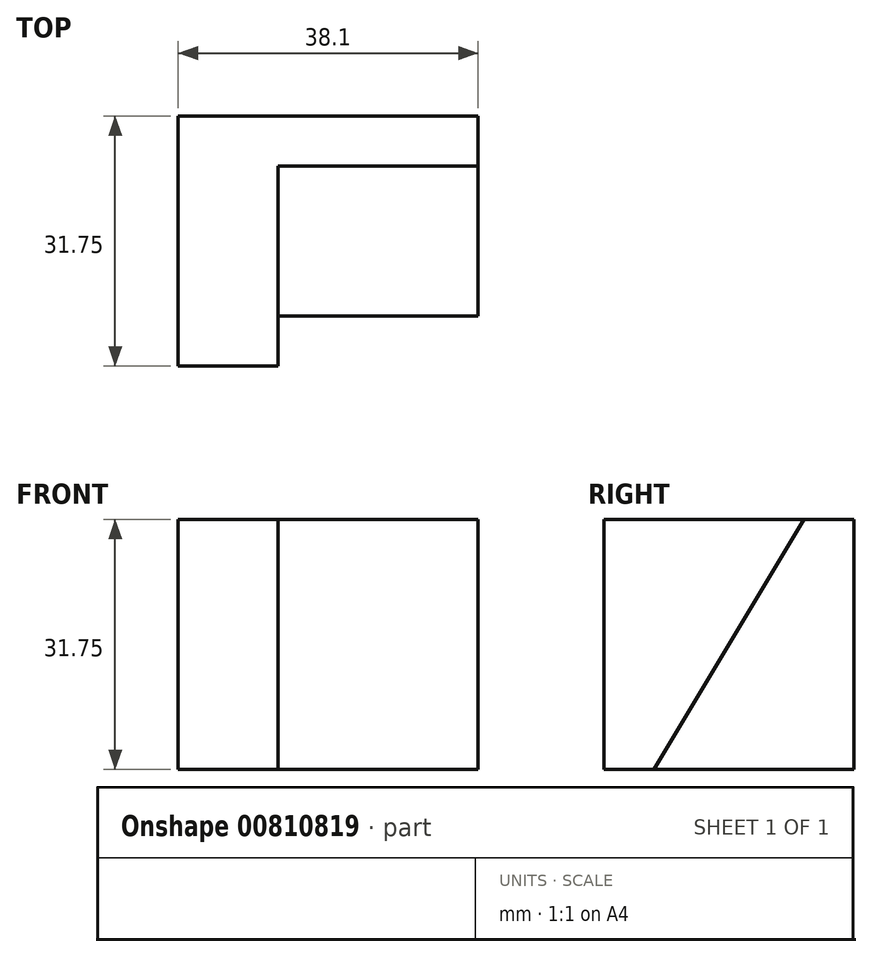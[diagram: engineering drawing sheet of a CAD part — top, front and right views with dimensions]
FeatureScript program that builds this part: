
annotation { "Feature Type Name" : "Feature", "Feature Type Description" : "" }
export const myFeature = defineFeature(function(context is Context, id is Id, definition is map)
    precondition{}
    {
        {
            var Q0;
            Q0=qCreatedBy(makeId("Top.planeOp"),FACE);
            var sketch = newSketch(context, id + "F0", { "sketchPlane" : qUnion([Q0])});
            skLineSegment(sketch, "E0", {"start": v(0, 0) * mm, "end": v(0, 31.75) * mm});
            skLineSegment(sketch, "E1", {"start": v(0, 0) * mm, "end": v(38.1, 0) * mm});
            skLineSegment(sketch, "E2", {"start": v(38.1, 0) * mm, "end": v(38.1, 31.75) * mm});
            skLineSegment(sketch, "E3", {"start": v(38.1, 31.75) * mm, "end": v(0, 31.75) * mm});
            skSolve(sketch);
        }
        {
            var Q0;
            Q0 = qSketchRegion(id + "F0", true);
            extrude(context, id + "F1", {"entities" : qUnion([Q0]), "depth" : 31.75 * mm, "offsetDistance" : 25.4 * mm});
        }
        {
            var Q0;
            Q0=makeQuery(id+"F1.opExtrude","SWEPT_FACE",FACE,{"disambiguationData":[OSD([sQuery(id+"F0.wireOp",EDGE,"E2")])]});
            var sketch = newSketch(context, id + "F2", { "sketchPlane" : qUnion([Q0])});
            skLineSegment(sketch, "E4", {"start": v(31.75, 31.75) * mm, "end": v(25.4, 31.75) * mm});
            skLineSegment(sketch, "E5", {"start": v(0, 0) * mm, "end": v(6.35, 0) * mm});
            skLineSegment(sketch, "E6", {"start": v(25.4, 31.75) * mm, "end": v(6.35, 0) * mm});
            skSolve(sketch);
        }
        {
            var Q0;
            Q0 = qSketchRegion(id + "F2", true);
            var Q1;
            Q1=makeQuery(id+"F2.imprint","IMPRINT",FACE,{"disambiguationData":[TD([[makeQuery(id+"F2.imprint","IMPRINT",EDGE,{"derivedFrom":sQuery(id+"F2.wireOp",EDGE,"E5")}),1.0]])]});
            extrude(context, id + "F3", {"entities" : qUnion([Q0, Q1]), "operationType" : NewBodyOperationType.REMOVE, "oppositeDirection" : true, "depth" : 25.4 * mm, "offsetDistance" : 25.4 * mm});
        }
    });
